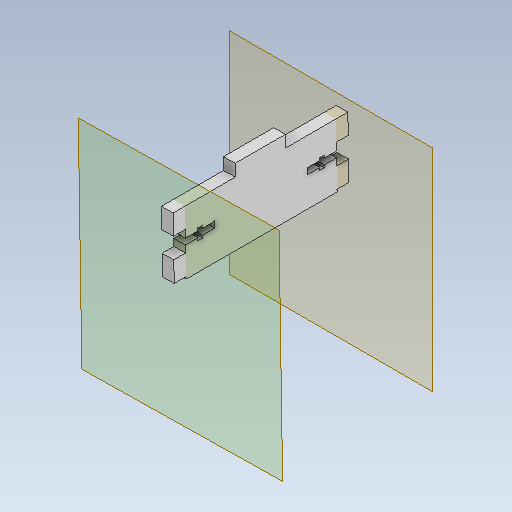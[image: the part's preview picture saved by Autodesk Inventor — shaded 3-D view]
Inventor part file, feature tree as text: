
AUTODESK INVENTOR PART (.ipt)
format: ipt  version: 2021.1 (Build 251245010, 245A)  size: 186,880 bytes
history: native  units: mm
features: reference x18, other x8, extrude x5, sketch x5, projected_geometry x1
ambient origin geometry x8: Origin, YZ Plane, XZ Plane, XY Plane, X Axis, Y Axis, Z Axis, Center Point
bodies: Body1 (feature_tree)
feature tree (37):
  other  "Твердое тело1"
  other  "РабПлоскость1"
  extrude  "Выдавливание1"  Depth=6.0mm
  other  "РабПлоскость2"
  extrude  "Выдавливание2"  TaperAngle=0.0deg  [1 undecoded]
  extrude  "Выдавливание3"  Depth=6.0mm
  extrude  "Выдавливание4"  TaperAngle=0.0deg  [1 undecoded]
  extrude  "Выдавливание5"  Depth=6.0mm
  sketch  "Эскиз1"
  sketch  "Эскиз2"
  sketch  "Эскиз3"
  reference  "Ссылка11"
  reference  "Ссылка12"
  projected_geometry  "Спроецированная петля1"
  sketch  "Эскиз4"
  reference  "Ссылка30"
  reference  "Ссылка31"
  sketch  "Эскиз5"
  reference  "Ссылка32"
  reference  "Ссылка33"
  reference  "Ссылка34"
  reference  "Ссылка35"
  reference  "Ссылка36"
  reference  "Ссылка37"
  reference  "Ссылка38"
  reference  "Ссылка39"
  reference  "Ссылка40"
  reference  "Ссылка41"
  reference  "Ссылка42"
  reference  "Ссылка43"
  reference  "Ссылка44"
  reference  "Ссылка45"
  other  "<userpath>\Documents\Savka\3d\Korp.iam"
  other  "Korp.iam"
  other  "Деталь1:1"
  other  "Korpus 5:1"
  other  "Korpus 3:1"
note: 2 required parameter values undecoded (feature->parameter linkage not recoverable at this tier; creation-order binding heuristic only, values carry confidence <= 0.55)
